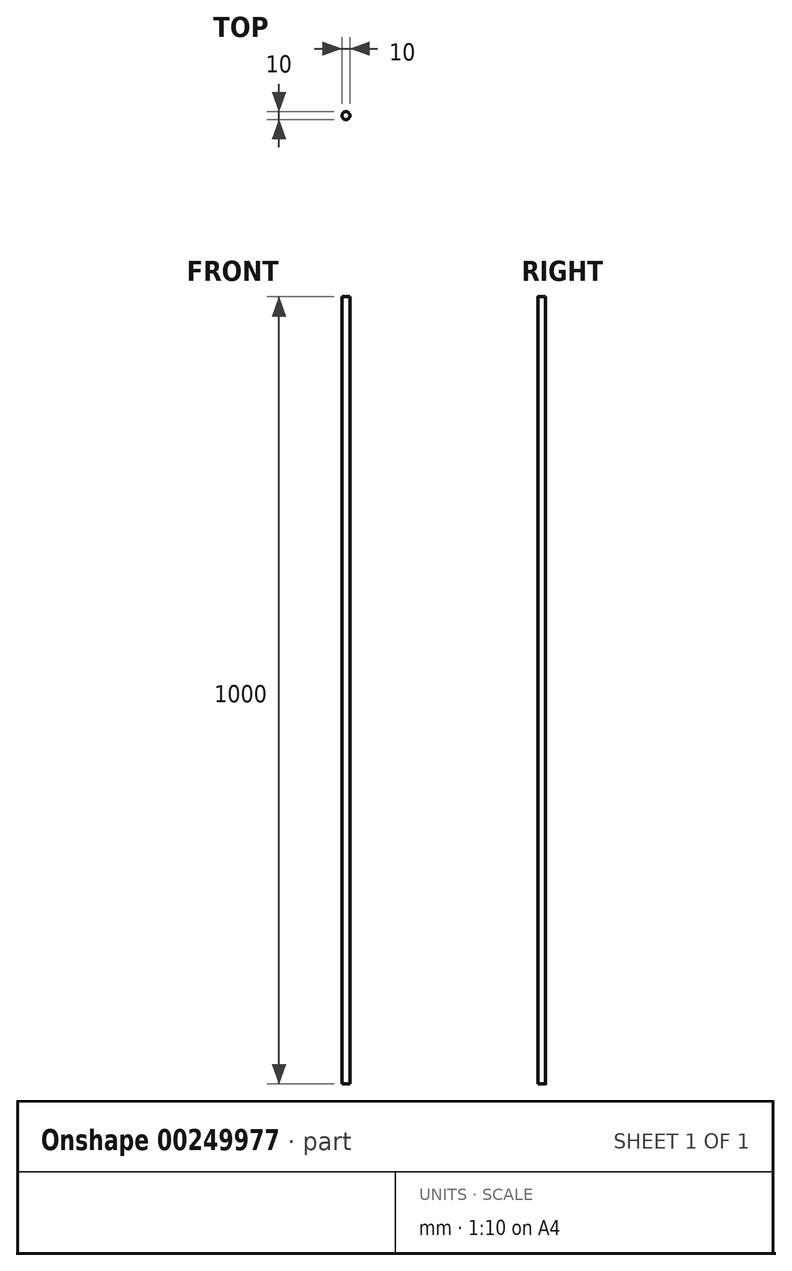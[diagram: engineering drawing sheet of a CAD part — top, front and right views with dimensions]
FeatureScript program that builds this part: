
annotation { "Feature Type Name" : "Feature", "Feature Type Description" : "" }
export const myFeature = defineFeature(function(context is Context, id is Id, definition is map)
    precondition{}
    {
        {
            var Q0;
            Q0=qCreatedBy(makeId("Top.planeOp"),FACE);
            var sketch = newSketch(context, id + "F0", { "sketchPlane" : qUnion([Q0])});
            skCircle(sketch, "E0", {"center": v(0, 0) * mm, "radius": 5 * mm});
            skSolve(sketch);
        }
        {
            var Q0;
            Q0 = qSketchRegion(id + "F0", true);
            extrude(context, id + "F1", {"entities" : qUnion([Q0]), "depth" : 1000 * mm});
        }
    });
